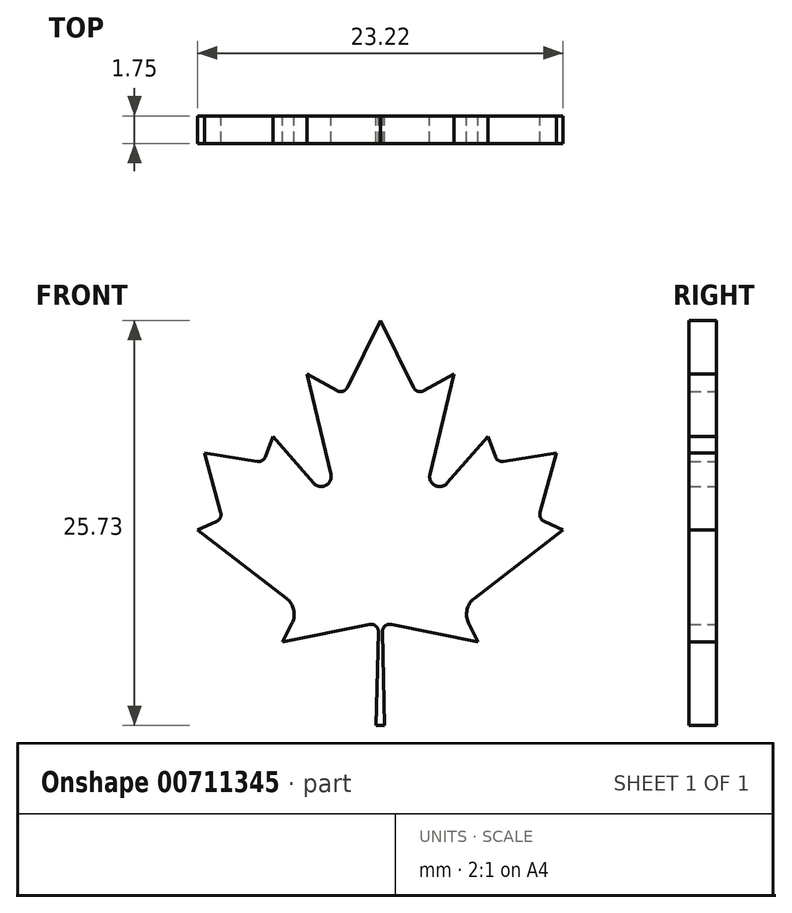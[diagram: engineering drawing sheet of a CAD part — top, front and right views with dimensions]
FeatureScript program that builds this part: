
annotation { "Feature Type Name" : "Feature", "Feature Type Description" : "" }
export const myFeature = defineFeature(function(context is Context, id is Id, definition is map)
    precondition{}
    {
        {
            var Q0;
            Q0=qCreatedBy(makeId("Front.planeOp"),FACE);
            var sketch = newSketch(context, id + "F0", { "sketchPlane" : qUnion([Q0])});
            skLineSegment(sketch, "E0", {"start": v(0.35, 19.11) * mm, "end": v(0.35, -3.5) * mm});
            skLineSegment(sketch, "E1", {"start": v(0.35, 19.11) * mm, "end": v(2.03, 15.7) * mm});
            skLineSegment(sketch, "E2", {"start": v(2.56, 15.54) * mm, "end": v(4.1, 16.4) * mm});
            skLineSegment(sketch, "E3", {"start": v(4.1, 16.4) * mm, "end": v(2.87, 11.3) * mm});
            skLineSegment(sketch, "E4", {"start": v(3.75, 10.85) * mm, "end": v(5.8, 13.22) * mm});
            skLineSegment(sketch, "E5", {"start": v(5.8, 13.22) * mm, "end": v(6.2, 12.2) * mm});
            skLineSegment(sketch, "E6", {"start": v(6.61, 11.95) * mm, "end": v(9.3, 12.37) * mm});
            skLineSegment(sketch, "E7", {"start": v(9.3, 12.37) * mm, "end": v(8.47, 9.35) * mm});
            skLineSegment(sketch, "E8", {"start": v(8.68, 8.9) * mm, "end": v(9.64, 8.47) * mm});
            skLineSegment(sketch, "E9", {"start": v(9.64, 8.47) * mm, "end": v(5.13, 5) * mm});
            skLineSegment(sketch, "E10", {"start": v(4.84, 3.74) * mm, "end": v(5.32, 2.78) * mm});
            skLineSegment(sketch, "E11", {"start": v(5.32, 2.78) * mm, "end": v(0.91, 3.67) * mm});
            skLineSegment(sketch, "E12", {"start": v(0.46, 3.3) * mm, "end": v(0.56, -1.47) * mm});
            skLineSegment(sketch, "E13", {"start": v(0.56, -1.47) * mm, "end": v(0.35, -1.47) * mm});
            skArc(sketch, "E14", {"start": v(2.03, 15.7) * mm, "mid": v(2.26, 15.51) * mm, "end": v(2.56, 15.54) * mm});
            skArc(sketch, "E15", {"start": v(2.87, 11.3) * mm, "mid": v(3.13, 10.73) * mm, "end": v(3.75, 10.85) * mm});
            skArc(sketch, "E16", {"start": v(6.2, 12.2) * mm, "mid": v(6.36, 12) * mm, "end": v(6.61, 11.95) * mm});
            skArc(sketch, "E17", {"start": v(8.47, 9.35) * mm, "mid": v(8.5, 9.09) * mm, "end": v(8.68, 8.9) * mm});
            skArc(sketch, "E18", {"start": v(5.13, 5) * mm, "mid": v(4.76, 4.42) * mm, "end": v(4.84, 3.74) * mm});
            skArc(sketch, "E19", {"start": v(0.91, 3.67) * mm, "mid": v(0.6, 3.6) * mm, "end": v(0.46, 3.3) * mm});
            skLineSegment(sketch, "E20", {"start": v(0.35, 19.11) * mm, "end": v(-1.33, 15.7) * mm});
            skArc(sketch, "E21", {"start": v(-1.86, 15.54) * mm, "mid": v(-1.56, 15.51) * mm, "end": v(-1.33, 15.7) * mm});
            skLineSegment(sketch, "E22", {"start": v(-1.86, 15.54) * mm, "end": v(-3.39, 16.4) * mm});
            skLineSegment(sketch, "E23", {"start": v(-3.39, 16.4) * mm, "end": v(-2.16, 11.3) * mm});
            skLineSegment(sketch, "E24", {"start": v(-3.04, 10.85) * mm, "end": v(-5.1, 13.22) * mm});
            skArc(sketch, "E25", {"start": v(-3.04, 10.85) * mm, "mid": v(-2.43, 10.73) * mm, "end": v(-2.16, 11.3) * mm});
            skLineSegment(sketch, "E26", {"start": v(-5.1, 13.22) * mm, "end": v(-5.5, 12.2) * mm});
            skLineSegment(sketch, "E27", {"start": v(-5.9, 11.95) * mm, "end": v(-8.6, 12.37) * mm});
            skArc(sketch, "E28", {"start": v(-5.9, 11.95) * mm, "mid": v(-5.66, 12) * mm, "end": v(-5.5, 12.2) * mm});
            skLineSegment(sketch, "E29", {"start": v(-8.6, 12.37) * mm, "end": v(-7.76, 9.35) * mm});
            skLineSegment(sketch, "E30", {"start": v(-7.98, 8.9) * mm, "end": v(-8.94, 8.47) * mm});
            skArc(sketch, "E31", {"start": v(-7.98, 8.9) * mm, "mid": v(-7.79, 9.09) * mm, "end": v(-7.76, 9.35) * mm});
            skLineSegment(sketch, "E32", {"start": v(-8.94, 8.47) * mm, "end": v(-4.42, 5) * mm});
            skArc(sketch, "E33", {"start": v(-4.14, 3.74) * mm, "mid": v(-4.05, 4.42) * mm, "end": v(-4.42, 5) * mm});
            skLineSegment(sketch, "E34", {"start": v(-4.14, 3.74) * mm, "end": v(-4.61, 2.78) * mm});
            skLineSegment(sketch, "E35", {"start": v(-4.61, 2.78) * mm, "end": v(-0.2, 3.67) * mm});
            skArc(sketch, "E36", {"start": v(0.25, 3.3) * mm, "mid": v(0.11, 3.6) * mm, "end": v(-0.2, 3.67) * mm});
            skLineSegment(sketch, "E37", {"start": v(0.25, 3.3) * mm, "end": v(0.14, -1.47) * mm});
            skLineSegment(sketch, "E38", {"start": v(0.14, -1.47) * mm, "end": v(0.35, -1.47) * mm});
            skSolve(sketch);
        }
        {
            var Q0;
            Q0=qSketchRegion(id+"F0",true);
            extrude(context, id + "F1", {"entities" : qUnion([Q0]), "depth" : 1.4 * mm, "offsetDistance" : 25 * mm});
        }
        {
            var Q0;
            Q0=makeQuery(id+"F1.opExtrude","SWEPT_BODY",BODY,{"disambiguationData":[OSD([sQuery(id+"F0.wireOp",EDGE,"E1"),sQuery(id+"F0.wireOp",EDGE,"E2"),sQuery(id+"F0.wireOp",EDGE,"E3"),sQuery(id+"F0.wireOp",EDGE,"E4"),sQuery(id+"F0.wireOp",EDGE,"E5"),sQuery(id+"F0.wireOp",EDGE,"E6"),sQuery(id+"F0.wireOp",EDGE,"E7"),sQuery(id+"F0.wireOp",EDGE,"E8"),sQuery(id+"F0.wireOp",EDGE,"E9"),sQuery(id+"F0.wireOp",EDGE,"E10"),sQuery(id+"F0.wireOp",EDGE,"E11"),sQuery(id+"F0.wireOp",EDGE,"E12"),sQuery(id+"F0.wireOp",EDGE,"E13"),sQuery(id+"F0.wireOp",EDGE,"E14"),sQuery(id+"F0.wireOp",EDGE,"E15"),sQuery(id+"F0.wireOp",EDGE,"E16"),sQuery(id+"F0.wireOp",EDGE,"E17"),sQuery(id+"F0.wireOp",EDGE,"E18"),sQuery(id+"F0.wireOp",EDGE,"E19"),sQuery(id+"F0.wireOp",EDGE,"E20"),sQuery(id+"F0.wireOp",EDGE,"E21"),sQuery(id+"F0.wireOp",EDGE,"E22"),sQuery(id+"F0.wireOp",EDGE,"E23"),sQuery(id+"F0.wireOp",EDGE,"E24"),sQuery(id+"F0.wireOp",EDGE,"E25"),sQuery(id+"F0.wireOp",EDGE,"E26"),sQuery(id+"F0.wireOp",EDGE,"E27"),sQuery(id+"F0.wireOp",EDGE,"E28"),sQuery(id+"F0.wireOp",EDGE,"E29"),sQuery(id+"F0.wireOp",EDGE,"E30"),sQuery(id+"F0.wireOp",EDGE,"E31"),sQuery(id+"F0.wireOp",EDGE,"E32"),sQuery(id+"F0.wireOp",EDGE,"E33"),sQuery(id+"F0.wireOp",EDGE,"E34"),sQuery(id+"F0.wireOp",EDGE,"E35"),sQuery(id+"F0.wireOp",EDGE,"E36"),sQuery(id+"F0.wireOp",EDGE,"E37"),sQuery(id+"F0.wireOp",EDGE,"E38")])]});
            var Q1;
            Q1=makeQuery(id+"F1.opExtrude","CAP_VERTEX",VERTEX,{"disambiguationData":[OSD([sQuery(id+"F0.wireOp",EDGE,"E0"),sQuery(id+"F0.wireOp",EDGE,"E1"),sQuery(id+"F0.wireOp",EDGE,"E20")])],"isStart":false});
            transform(context, id + "F2", {"entities" : qUnion([Q0]), "transformType" : TransformType.SCALE_UNIFORMLY, "scale" : 1.25, "scalePoint" : qUnion([Q1]), "makeCopy" : false});
        }
    });
